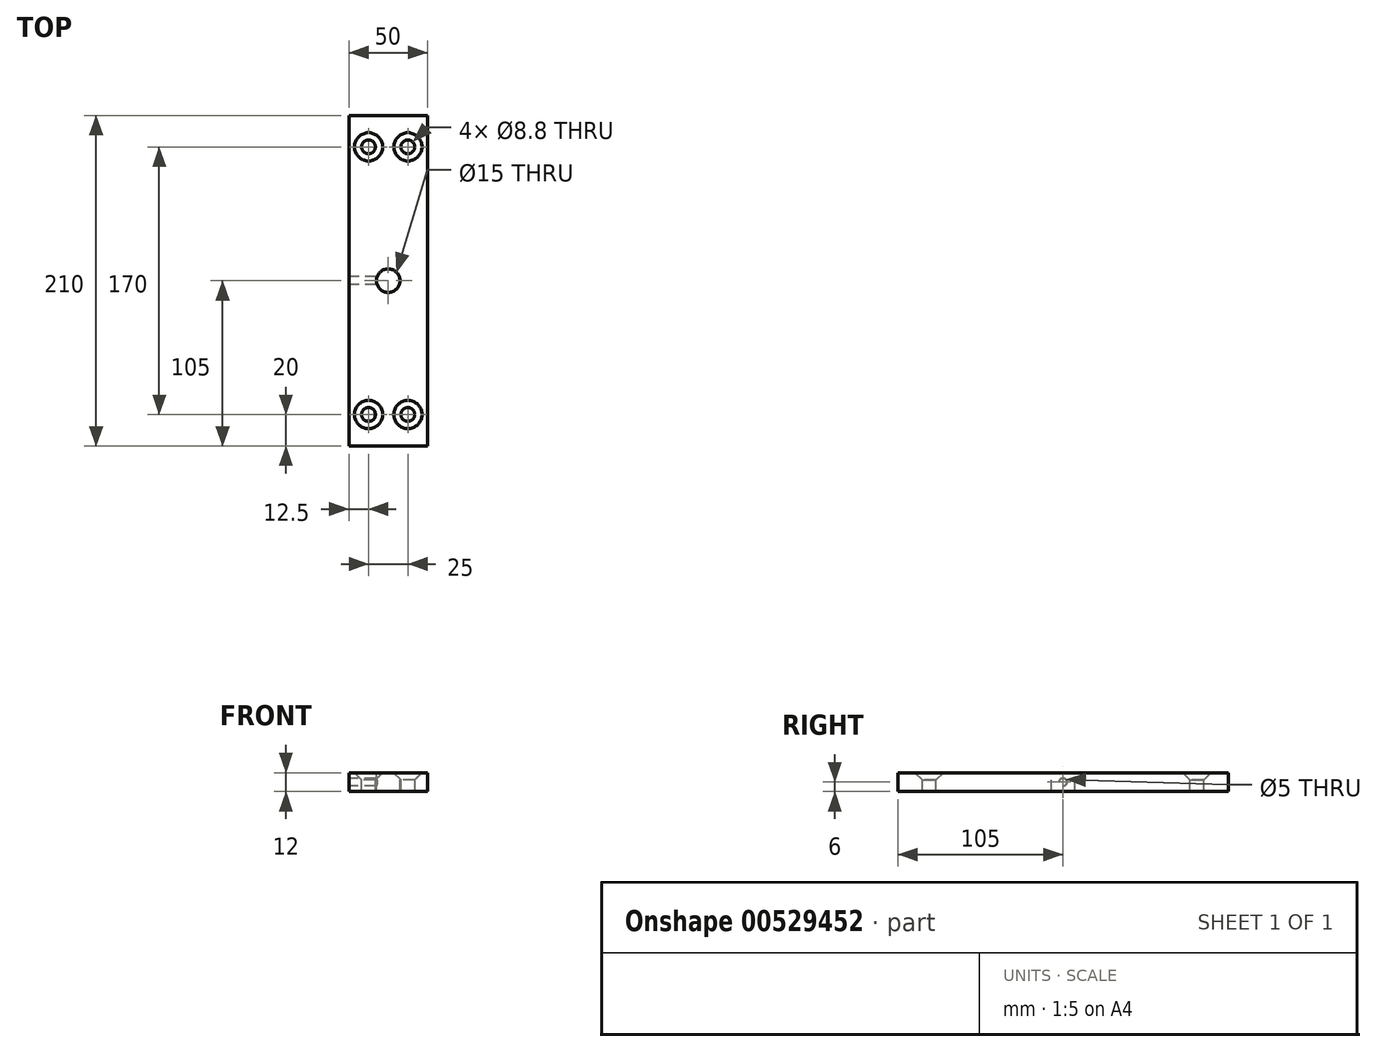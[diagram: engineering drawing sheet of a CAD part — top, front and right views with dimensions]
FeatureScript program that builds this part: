
annotation { "Feature Type Name" : "Feature", "Feature Type Description" : "" }
export const myFeature = defineFeature(function(context is Context, id is Id, definition is map)
    precondition{}
    {
        {
            var Q0;
            Q0=qCreatedBy(makeId("Top.planeOp"),FACE);
            var sketch = newSketch(context, id + "F0", { "sketchPlane" : qUnion([Q0])});
            skLineSegment(sketch, "E0.bottom", {"start": v(0, 0) * mm, "end": v(50, 0) * mm});
            skLineSegment(sketch, "E0.top", {"start": v(0, 210) * mm, "end": v(50, 210) * mm});
            skLineSegment(sketch, "E0.left", {"start": v(0, 0) * mm, "end": v(0, 210) * mm});
            skLineSegment(sketch, "E0.right", {"start": v(50, 0) * mm, "end": v(50, 210) * mm});
            skSolve(sketch);
        }
        {
            var Q0;
            Q0 = qSketchRegion(id + "F0", true);
            extrude(context, id + "F1", {"entities" : qUnion([Q0]), "oppositeDirection" : true, "depth" : 12 * mm, "offsetDistance" : 25 * mm});
        }
        {
            var Q0;
            Q0=qCreatedBy(makeId("Top.planeOp"),FACE);
            var sketch = newSketch(context, id + "F2", { "sketchPlane" : qUnion([Q0])});
            skPoint(sketch, "E1", {"position": v(12.5, 20) * mm});
            skPoint(sketch, "E2", {"position": v(37.5, 20) * mm});
            skLineSegment(sketch, "E3", {"start": v(25, 0) * mm, "end": v(25, 210) * mm, "construction": true});
            skPoint(sketch, "E4", {"position": v(12.5, 190) * mm});
            skPoint(sketch, "E5", {"position": v(37.5, 190) * mm});
            skLineSegment(sketch, "E6", {"start": v(25, 105) * mm, "end": v(0, 105) * mm, "construction": true});
            skSolve(sketch);
        }
        {
            var Q0;
            Q0=sQuery(id+"F2.wireOp",VERTEX,"E1");
            var Q1;
            Q1=sQuery(id+"F2.wireOp",VERTEX,"E2");
            var Q2;
            Q2=sQuery(id+"F2.wireOp",VERTEX,"E5");
            var Q3;
            Q3=sQuery(id+"F2.wireOp",VERTEX,"E4");
            var Q4;
            Q4=makeQuery(id+"F1.opExtrude","SWEPT_BODY",BODY,{"disambiguationData":[OSD([sQuery(id+"F0.wireOp",EDGE,"E0.bottom"),sQuery(id+"F0.wireOp",EDGE,"E0.top"),sQuery(id+"F0.wireOp",EDGE,"E0.left"),sQuery(id+"F0.wireOp",EDGE,"E0.right")])]});
            hole(context, id + "F3", {"style" : HoleStyle.C_SINK, "endStyle" : HoleEndStyle.THROUGH, "standardTappedOrClearance" : lookupTablePath({ "standard" : "ISO", "fit" : "Normal", "size" : "M8", "type" : "Clearance" }), "standardBlindInLast" : lookupTablePath({ "fit" : "Standard", "standard" : "ISO", "size" : "M8", "type" : "Clearance" }), "holeDiameter" : 8.8 * mm, "cSinkDiameter" : 17.92 * mm, "cSinkAngle" : 90 * degree, "isTappedThrough" : true, "tappedDepth" : 12 * mm, "tapClearance" : 3, "locations" : qUnion([Q0, Q1, Q2, Q3]), "scope" : qUnion([Q4])});
        }
        {
            var Q0;
            Q0=makeQuery(id+"F1.opExtrude","CAP_FACE",FACE,{"disambiguationData":[OSD([sQuery(id+"F0.wireOp",EDGE,"E0.bottom"),sQuery(id+"F0.wireOp",EDGE,"E0.top"),sQuery(id+"F0.wireOp",EDGE,"E0.left"),sQuery(id+"F0.wireOp",EDGE,"E0.right")])],"isStart":true});
            var sketch = newSketch(context, id + "F4", { "sketchPlane" : qUnion([Q0])});
            skLineSegment(sketch, "E7", {"start": v(25, 210) * mm, "end": v(25, 0) * mm, "construction": true});
            skPoint(sketch, "E8", {"position": v(25, 105) * mm});
            skSolve(sketch);
        }
        {
            var Q0;
            Q0=sQuery(id+"F4.wireOp",VERTEX,"E8");
            var Q1;
            Q1=makeQuery(id+"F1.opExtrude","SWEPT_BODY",BODY,{"disambiguationData":[OSD([sQuery(id+"F0.wireOp",EDGE,"E0.bottom"),sQuery(id+"F0.wireOp",EDGE,"E0.top"),sQuery(id+"F0.wireOp",EDGE,"E0.left"),sQuery(id+"F0.wireOp",EDGE,"E0.right")])]});
            hole(context, id + "F5", {"style" : HoleStyle.SIMPLE, "endStyle" : HoleEndStyle.THROUGH, "holeDiameter" : 15 * mm, "isTappedThrough" : true, "tappedDepth" : 12 * mm, "tapClearance" : 3, "locations" : qUnion([Q0]), "scope" : qUnion([Q1])});
        }
        {
            var Q0;
            Q0=makeQuery(id+"F1.opExtrude","SWEPT_FACE",FACE,{"disambiguationData":[OSD([sQuery(id+"F0.wireOp",EDGE,"E0.left")])]});
            var sketch = newSketch(context, id + "F6", { "sketchPlane" : qUnion([Q0])});
            skLineSegment(sketch, "E9", {"start": v(-210, -6) * mm, "end": v(0, -6) * mm});
            skPoint(sketch, "E10", {"position": v(-105, -6) * mm});
            skSolve(sketch);
        }
        {
            var Q0;
            Q0=sQuery(id+"F6.wireOp",VERTEX,"E10");
            var Q1;
            Q1=makeQuery(id+"F1.opExtrude","SWEPT_BODY",BODY,{"disambiguationData":[OSD([sQuery(id+"F0.wireOp",EDGE,"E0.bottom"),sQuery(id+"F0.wireOp",EDGE,"E0.top"),sQuery(id+"F0.wireOp",EDGE,"E0.left"),sQuery(id+"F0.wireOp",EDGE,"E0.right")])]});
            hole(context, id + "F7", {"style" : HoleStyle.SIMPLE, "endStyle" : HoleEndStyle.BLIND, "standardTappedOrClearance" : lookupTablePath({ "standard" : "ISO", "engagement" : "75%", "pitch" : "1 mm", "size" : "M6", "type" : "Tapped" }), "standardBlindInLast" : lookupTablePath({ "standard" : "ISO", "engagement" : "75%", "pitch" : "1 mm", "size" : "M6", "type" : "Tapped" }), "holeDiameter" : 5 * mm, "showTappedDepth" : true, "holeDepth" : 20 * mm, "isTappedThrough" : true, "tappedDepth" : 17 * mm, "tapClearance" : 3, "locations" : qUnion([Q0]), "scope" : qUnion([Q1]), "majorDiameter" : 6 * mm});
        }
    });
